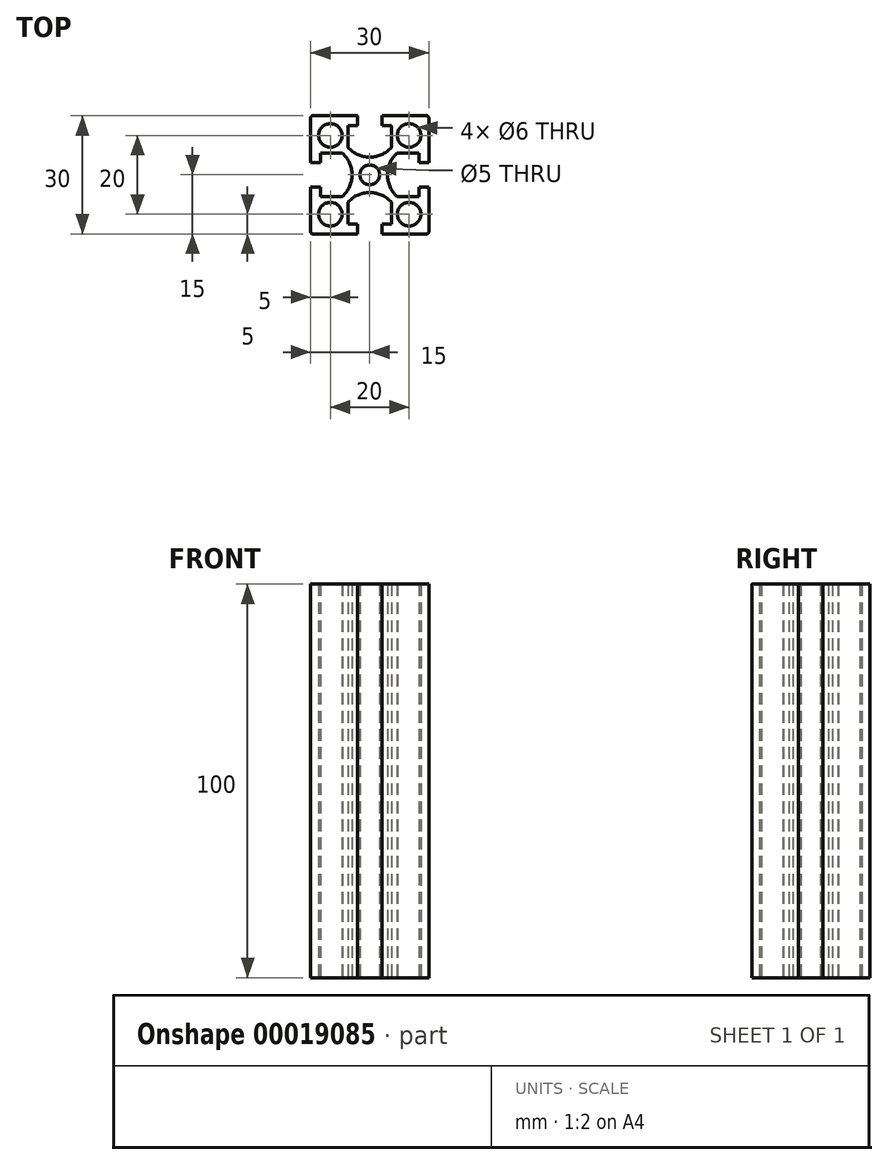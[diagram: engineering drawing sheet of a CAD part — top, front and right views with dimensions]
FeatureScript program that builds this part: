
annotation { "Feature Type Name" : "Feature", "Feature Type Description" : "" }
export const myFeature = defineFeature(function(context is Context, id is Id, definition is map)
    precondition{}
    {
        {
            var Q0;
            Q0=qCreatedBy(makeId("Top.planeOp"),FACE);
            var sketch = newSketch(context, id + "F0", { "sketchPlane" : qUnion([Q0])});
            skCircle(sketch, "E0", {"center": v(0, 0) * mm, "radius": 2.5 * mm});
            skLineSegment(sketch, "E1", {"start": v(0, 0) * mm, "end": v(-15, 0) * mm, "construction": true});
            skLineSegment(sketch, "E2", {"start": v(-15, 0) * mm, "end": v(-15, 15) * mm, "construction": true});
            skLineSegment(sketch, "E3", {"start": v(-15, 15) * mm, "end": v(0, 15) * mm, "construction": true});
            skLineSegment(sketch, "E4", {"start": v(0, 15) * mm, "end": v(0, 0) * mm, "construction": true});
            skLineSegment(sketch, "E5", {"start": v(-15, 15) * mm, "end": v(0, 0) * mm, "construction": true});
            skLineSegment(sketch, "E6", {"start": v(-15, 10) * mm, "end": v(-10, 10) * mm, "construction": true});
            skPoint(sketch, "E7", {"position": v(-15, 3.15) * mm});
            skPoint(sketch, "E8", {"position": v(-15, 5.5) * mm});
            skCircle(sketch, "E9", {"center": v(-10, 10) * mm, "radius": 3 * mm});
            skLineSegment(sketch, "E10", {"start": v(-15, 14.5) * mm, "end": v(-15, 3.15) * mm});
            skLineSegment(sketch, "E11", {"start": v(-15, 3.15) * mm, "end": v(-12.5, 3.15) * mm});
            skLineSegment(sketch, "E12", {"start": v(-12.5, 3.15) * mm, "end": v(-12.5, 5.5) * mm});
            skPoint(sketch, "E13", {"position": v(-4.5, 0) * mm});
            skLineSegment(sketch, "E14", {"start": v(-12.5, 5.5) * mm, "end": v(-5.5, 5.5) * mm, "construction": true});
            skArc(sketch, "E15", {"start": v(-4.5, 0) * mm, "mid": v(-5.13, 3) * mm, "end": v(-6.9, 5.5) * mm});
            skLineSegment(sketch, "E16", {"start": v(-12.5, 5.5) * mm, "end": v(-6.9, 5.5) * mm});
            skLineSegment(sketch, "E17.0.MirrorCS", {"start": v(-14.5, 15) * mm, "end": v(-3.15, 15) * mm});
            skPoint(sketch, "E18.visualSharp", {"position": v(-15, 15) * mm});
            skArc(sketch, "E18.filletArc", {"start": v(-14.5, 15) * mm, "mid": v(-14.85, 14.85) * mm, "end": v(-15, 14.5) * mm});
            skLineSegment(sketch, "E19.0.MirrorCS", {"start": v(-3.15, 15) * mm, "end": v(-3.15, 12.5) * mm});
            skLineSegment(sketch, "E20.0.MirrorCS", {"start": v(-3.15, 12.5) * mm, "end": v(-5.5, 12.5) * mm});
            skLineSegment(sketch, "E21.0.MirrorCS", {"start": v(-5.5, 12.5) * mm, "end": v(-5.5, 6.9) * mm});
            skArc(sketch, "E22.0.MirrorCS", {"start": v(0, 4.5) * mm, "mid": v(-3, 5.13) * mm, "end": v(-5.5, 6.9) * mm});
            skArc(sketch, "E23.0.MirrorCS", {"start": v(-4.5, 0) * mm, "mid": v(-5.13, -3) * mm, "end": v(-6.9, -5.5) * mm});
            skLineSegment(sketch, "E24.0.MirrorCS", {"start": v(-12.5, -5.5) * mm, "end": v(-6.9, -5.5) * mm});
            skLineSegment(sketch, "E25.0.MirrorCS", {"start": v(-12.5, -3.15) * mm, "end": v(-12.5, -5.5) * mm});
            skLineSegment(sketch, "E26.0.MirrorCS", {"start": v(-15, -3.15) * mm, "end": v(-12.5, -3.15) * mm});
            skLineSegment(sketch, "E27.0.MirrorCS", {"start": v(-15, -14.5) * mm, "end": v(-15, -3.15) * mm});
            skArc(sketch, "E28.0.MirrorCS", {"start": v(-14.5, -15) * mm, "mid": v(-14.85, -14.85) * mm, "end": v(-15, -14.5) * mm});
            skLineSegment(sketch, "E29.0.MirrorCS", {"start": v(-14.5, -15) * mm, "end": v(-3.15, -15) * mm});
            skLineSegment(sketch, "E30.0.MirrorCS", {"start": v(-3.15, -15) * mm, "end": v(-3.15, -12.5) * mm});
            skLineSegment(sketch, "E31.0.MirrorCS", {"start": v(-3.15, -12.5) * mm, "end": v(-5.5, -12.5) * mm});
            skLineSegment(sketch, "E32.0.MirrorCS", {"start": v(-5.5, -12.5) * mm, "end": v(-5.5, -6.9) * mm});
            skArc(sketch, "E33.0.MirrorCS", {"start": v(0, -4.5) * mm, "mid": v(-3, -5.13) * mm, "end": v(-5.5, -6.9) * mm});
            skCircle(sketch, "E34.0.MirrorC", {"center": v(-10, -10) * mm, "radius": 3 * mm});
            skArc(sketch, "E35.0.MirrorCS", {"start": v(0, 4.5) * mm, "mid": v(3, 5.13) * mm, "end": v(5.5, 6.9) * mm});
            skLineSegment(sketch, "E36.0.MirrorCS", {"start": v(5.5, 12.5) * mm, "end": v(5.5, 6.9) * mm});
            skLineSegment(sketch, "E37.0.MirrorCS", {"start": v(3.15, 12.5) * mm, "end": v(5.5, 12.5) * mm});
            skLineSegment(sketch, "E38.0.MirrorCS", {"start": v(3.15, 15) * mm, "end": v(3.15, 12.5) * mm});
            skLineSegment(sketch, "E39.0.MirrorCS", {"start": v(14.5, 15) * mm, "end": v(3.15, 15) * mm});
            skArc(sketch, "E40.0.MirrorCS", {"start": v(14.5, 15) * mm, "mid": v(14.85, 14.85) * mm, "end": v(15, 14.5) * mm});
            skLineSegment(sketch, "E41.0.MirrorCS", {"start": v(15, 14.5) * mm, "end": v(15, 3.15) * mm});
            skLineSegment(sketch, "E42.0.MirrorCS", {"start": v(15, 3.15) * mm, "end": v(12.5, 3.15) * mm});
            skLineSegment(sketch, "E43.0.MirrorCS", {"start": v(12.5, 3.15) * mm, "end": v(12.5, 5.5) * mm});
            skLineSegment(sketch, "E44.0.MirrorCS", {"start": v(12.5, 5.5) * mm, "end": v(6.9, 5.5) * mm});
            skArc(sketch, "E45.0.MirrorCS", {"start": v(4.5, 0) * mm, "mid": v(5.13, 3) * mm, "end": v(6.9, 5.5) * mm});
            skArc(sketch, "E46.0.MirrorCS", {"start": v(4.5, 0) * mm, "mid": v(5.13, -3) * mm, "end": v(6.9, -5.5) * mm});
            skLineSegment(sketch, "E47.0.MirrorCS", {"start": v(12.5, -5.5) * mm, "end": v(6.9, -5.5) * mm});
            skLineSegment(sketch, "E48.0.MirrorCS", {"start": v(12.5, -3.15) * mm, "end": v(12.5, -5.5) * mm});
            skLineSegment(sketch, "E49.0.MirrorCS", {"start": v(15, -3.15) * mm, "end": v(12.5, -3.15) * mm});
            skLineSegment(sketch, "E50.0.MirrorCS", {"start": v(15, -14.5) * mm, "end": v(15, -3.15) * mm});
            skArc(sketch, "E51.0.MirrorCS", {"start": v(14.5, -15) * mm, "mid": v(14.85, -14.85) * mm, "end": v(15, -14.5) * mm});
            skLineSegment(sketch, "E52.0.MirrorCS", {"start": v(14.5, -15) * mm, "end": v(3.15, -15) * mm});
            skLineSegment(sketch, "E53.0.MirrorCS", {"start": v(3.15, -15) * mm, "end": v(3.15, -12.5) * mm});
            skLineSegment(sketch, "E54.0.MirrorCS", {"start": v(3.15, -12.5) * mm, "end": v(5.5, -12.5) * mm});
            skLineSegment(sketch, "E55.0.MirrorCS", {"start": v(5.5, -12.5) * mm, "end": v(5.5, -6.9) * mm});
            skArc(sketch, "E56.0.MirrorCS", {"start": v(0, -4.5) * mm, "mid": v(3, -5.13) * mm, "end": v(5.5, -6.9) * mm});
            skCircle(sketch, "E57.0.MirrorC", {"center": v(10, 10) * mm, "radius": 3 * mm});
            skCircle(sketch, "E58.0.MirrorC", {"center": v(10, -10) * mm, "radius": 3 * mm});
            skSolve(sketch);
        }
        {
            var Q0;
            Q0=makeQuery(id+"F0.imprint","IMPRINT",FACE,{"disambiguationData":[TD([[makeQuery(id+"F0.imprint","IMPRINT",EDGE,{"derivedFrom":sQuery(id+"F0.wireOp",EDGE,"E0")}),-1.0]])]});
            extrude(context, id + "F1", {"entities" : qUnion([Q0]), "depth" : 100 * mm});
        }
    });
